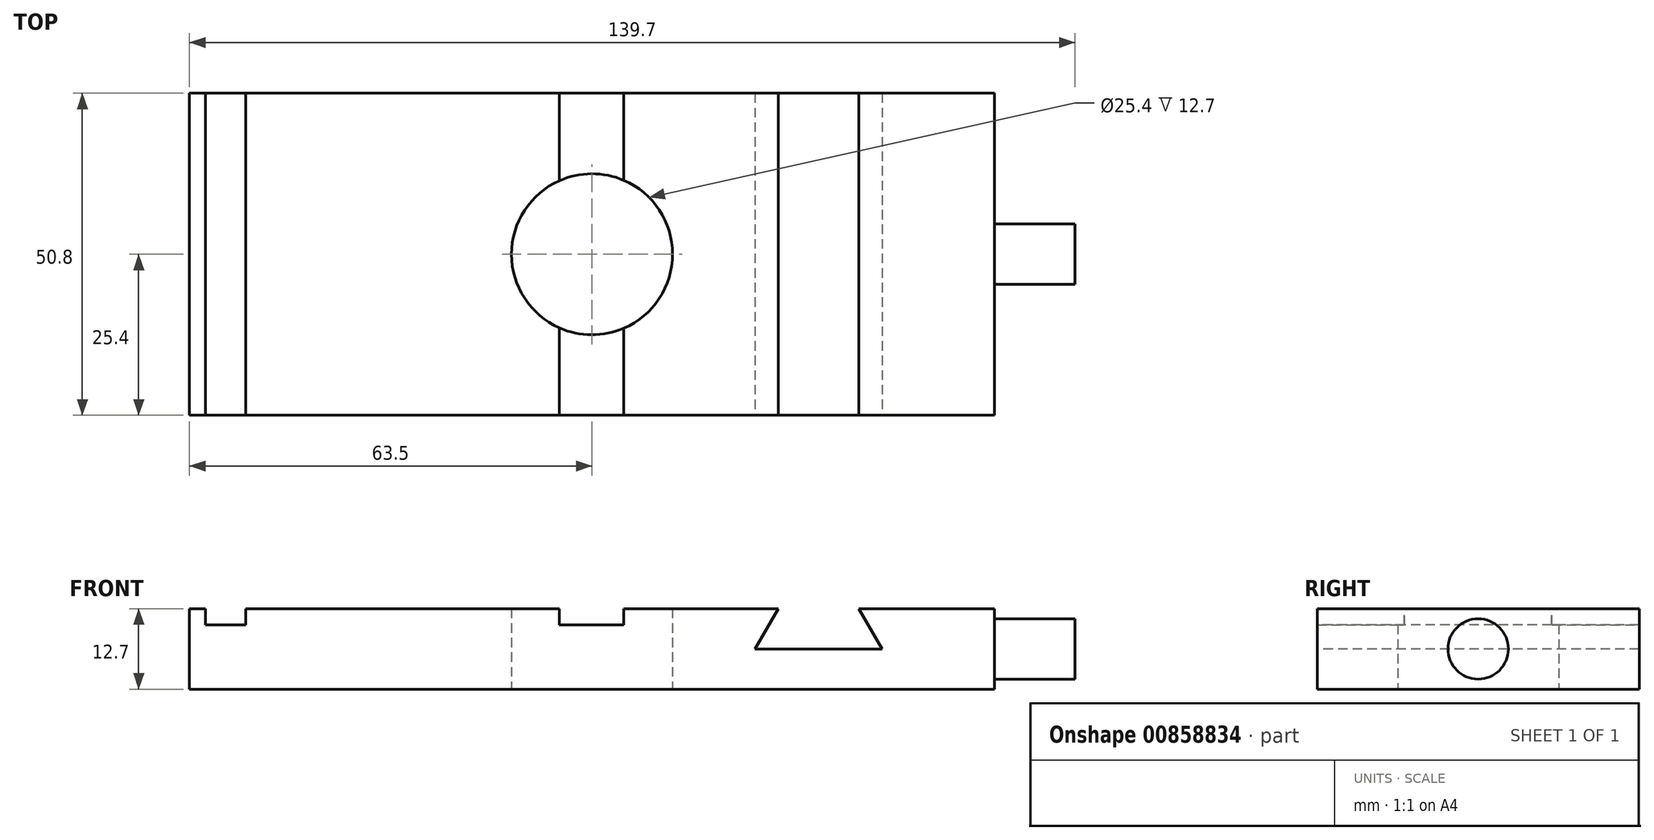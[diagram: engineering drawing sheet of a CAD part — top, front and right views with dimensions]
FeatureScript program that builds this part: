
annotation { "Feature Type Name" : "Feature", "Feature Type Description" : "" }
export const myFeature = defineFeature(function(context is Context, id is Id, definition is map)
    precondition{}
    {
        {
            var Q0;
            Q0=qCreatedBy(makeId("Top.planeOp"),FACE);
            var sketch = newSketch(context, id + "F0", { "sketchPlane" : qUnion([Q0])});
            skLineSegment(sketch, "E0.bottom", {"start": v(63.5, 25.4) * mm, "end": v(-63.5, 25.4) * mm});
            skLineSegment(sketch, "E0.top", {"start": v(63.5, -25.4) * mm, "end": v(-63.5, -25.4) * mm});
            skLineSegment(sketch, "E0.left", {"start": v(63.5, 25.4) * mm, "end": v(63.5, -25.4) * mm});
            skLineSegment(sketch, "E0.right", {"start": v(-63.5, 25.4) * mm, "end": v(-63.5, -25.4) * mm});
            skPoint(sketch, "E0.middle", {"position": v(0, 0) * mm});
            skCircle(sketch, "E1", {"center": v(0, 0) * mm, "radius": 12.7 * mm});
            skSolve(sketch);
        }
        {
            var Q0;
            Q0=makeQuery(id+"F0.imprint","IMPRINT",FACE,{"disambiguationData":[TD([[makeQuery(id+"F0.imprint","IMPRINT",EDGE,{"derivedFrom":sQuery(id+"F0.wireOp",EDGE,"E0.bottom")}),1.0]])]});
            extrude(context, id + "F1", {"entities" : qUnion([Q0]), "depth" : 12.7 * mm, "offsetDistance" : 25.4 * mm});
        }
        {
            var Q0;
            Q0=makeQuery(id+"F1.opExtrude","CAP_FACE",FACE,{"disambiguationData":[OSD([sQuery(id+"F0.wireOp",EDGE,"E0.bottom"),sQuery(id+"F0.wireOp",EDGE,"E0.top"),sQuery(id+"F0.wireOp",EDGE,"E0.left"),sQuery(id+"F0.wireOp",EDGE,"E0.right"),sQuery(id+"F0.wireOp",EDGE,"E1")])],"isStart":false});
            var sketch = newSketch(context, id + "F2", { "sketchPlane" : qUnion([Q0])});
            skLineSegment(sketch, "E2.bottom", {"start": v(-60.96, 25.4) * mm, "end": v(-54.6, 25.4) * mm});
            skLineSegment(sketch, "E2.top", {"start": v(-60.96, -25.4) * mm, "end": v(-54.6, -25.4) * mm});
            skLineSegment(sketch, "E2.left", {"start": v(-60.96, 25.4) * mm, "end": v(-60.96, -25.4) * mm});
            skLineSegment(sketch, "E2.right", {"start": v(-54.6, 25.4) * mm, "end": v(-54.6, -25.4) * mm});
            skLineSegment(sketch, "E3", {"start": v(-5.16, 25.4) * mm, "end": v(-5.16, -25.4) * mm});
            skLineSegment(sketch, "E4", {"start": v(-5.16, -25.4) * mm, "end": v(5, -25.4) * mm});
            skLineSegment(sketch, "E5", {"start": v(5, -25.4) * mm, "end": v(5, 25.4) * mm});
            skLineSegment(sketch, "E6", {"start": v(5, 25.4) * mm, "end": v(-5.16, 25.4) * mm});
            skPoint(sketch, "E7", {"position": v(0, 0) * mm});
            skLineSegment(sketch, "E8", {"start": v(0, 25.4) * mm, "end": v(0, -25.4) * mm, "construction": true});
            skSolve(sketch);
        }
        {
            var Q0;
            {var subQ0=sQuery(id+"F2.wireOp",EDGE,"E6");Q0=makeQuery(id+"F2.imprint","IMPRINT",FACE,{"disambiguationData":[TD([[makeQuery(id+"F2.imprint","IMPRINT",EDGE,{"derivedFrom":subQ0}),1.0]])]});}
            var Q1;
            {var subQ0=sQuery(id+"F2.wireOp",EDGE,"E4");Q1=makeQuery(id+"F2.imprint","IMPRINT",FACE,{"disambiguationData":[TD([[makeQuery(id+"F2.imprint","IMPRINT",EDGE,{"derivedFrom":subQ0}),-1.0]])]});}
            var Q2;
            Q2=makeQuery(id+"F2.imprint","IMPRINT",FACE,{"disambiguationData":[TD([[makeQuery(id+"F2.imprint","IMPRINT",EDGE,{"derivedFrom":sQuery(id+"F2.wireOp",EDGE,"E2.bottom")}),1.0]])]});
            extrude(context, id + "F3", {"entities" : qUnion([Q0, Q1, Q2]), "operationType" : NewBodyOperationType.REMOVE, "oppositeDirection" : true, "depth" : 2.54 * mm, "offsetDistance" : 25.4 * mm});
        }
        {
            var Q0;
            Q0=makeQuery(id+"F1.opExtrude","SWEPT_FACE",FACE,{"disambiguationData":[OSD([sQuery(id+"F0.wireOp",EDGE,"E0.top")])]});
            var sketch = newSketch(context, id + "F4", { "sketchPlane" : qUnion([Q0])});
            skLineSegment(sketch, "E9", {"start": v(29.37, 12.7) * mm, "end": v(25.7, 6.35) * mm});
            skLineSegment(sketch, "E10", {"start": v(25.7, 6.35) * mm, "end": v(45.74, 6.35) * mm});
            skLineSegment(sketch, "E11", {"start": v(45.74, 6.35) * mm, "end": v(42.07, 12.7) * mm});
            skLineSegment(sketch, "E12", {"start": v(42.07, 12.7) * mm, "end": v(29.37, 12.7) * mm});
            skLineSegment(sketch, "E13", {"start": v(35.72, 6.35) * mm, "end": v(35.72, 12.7) * mm, "construction": true});
            skSolve(sketch);
        }
        {
            var Q0;
            Q0=makeQuery(id+"F4.imprint","IMPRINT",FACE,{"disambiguationData":[TD([[makeQuery(id+"F4.imprint","IMPRINT",EDGE,{"derivedFrom":sQuery(id+"F4.wireOp",EDGE,"E9")}),1.0]])]});
            extrude(context, id + "F5", {"entities" : qUnion([Q0]), "operationType" : NewBodyOperationType.REMOVE, "endBound" : BoundingType.THROUGH_ALL, "oppositeDirection" : true, "depth" : 25.4 * mm, "offsetDistance" : 25.4 * mm});
        }
        {
            var Q0;
            Q0=makeQuery(id+"F1.opExtrude","SWEPT_FACE",FACE,{"disambiguationData":[OSD([sQuery(id+"F0.wireOp",EDGE,"E0.left")])]});
            var sketch = newSketch(context, id + "F6", { "sketchPlane" : qUnion([Q0])});
            skPoint(sketch, "E14", {"position": v(0, 6.35) * mm});
            skPoint(sketch, "E14.positionSnap0", {"position": v(-25.4, 6.35) * mm});
            skPoint(sketch, "E14.positionSnap1", {"position": v(0, 12.7) * mm});
            skCircle(sketch, "E15", {"center": v(0, 6.35) * mm, "radius": 4.76 * mm});
            skSolve(sketch);
        }
        {
            var Q0;
            Q0=makeQuery(id+"F6.imprint","IMPRINT",FACE,{"disambiguationData":[TD([[makeQuery(id+"F6.imprint","IMPRINT",EDGE,{"derivedFrom":sQuery(id+"F6.wireOp",EDGE,"E15")}),1.0]])]});
            extrude(context, id + "F7", {"entities" : qUnion([Q0]), "operationType" : NewBodyOperationType.ADD, "depth" : 12.7 * mm, "offsetDistance" : 25.4 * mm});
        }
    });
